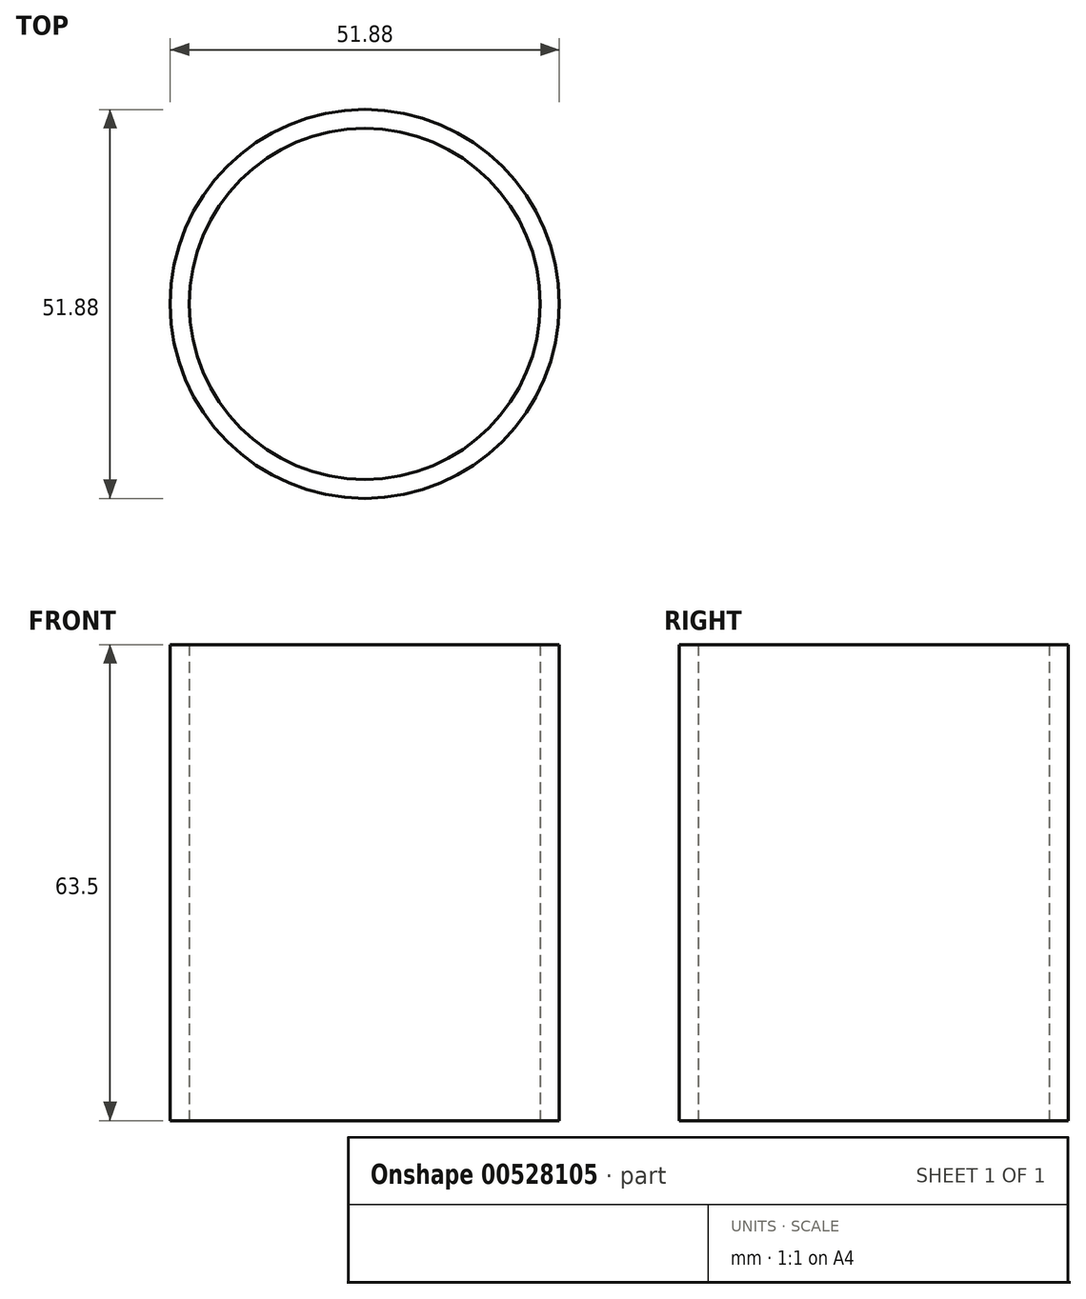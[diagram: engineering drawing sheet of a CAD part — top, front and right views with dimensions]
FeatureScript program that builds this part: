
annotation { "Feature Type Name" : "Feature", "Feature Type Description" : "" }
export const myFeature = defineFeature(function(context is Context, id is Id, definition is map)
    precondition{}
    {
        {
            var Q0;
            Q0=qCreatedBy(makeId("Top.planeOp"),FACE);
            var sketch = newSketch(context, id + "F0", { "sketchPlane" : qUnion([Q0])});
            skCircle(sketch, "E0", {"center": v(0, 0) * mm, "radius": 25.94 * mm});
            skSolve(sketch);
        }
        {
            var Q0;
            Q0=makeQuery(id+"F0.imprint","IMPRINT",FACE,{"disambiguationData":[TD([[makeQuery(id+"F0.imprint","IMPRINT",EDGE,{"derivedFrom":sQuery(id+"F0.wireOp",EDGE,"E0")}),1.0]])]});
            extrude(context, id + "F1", {"entities" : qUnion([Q0]), "depth" : 63.5 * mm, "offsetDistance" : 25.4 * mm});
        }
        {
            var Q0;
            Q0=makeQuery(id+"F1.opExtrude","CAP_FACE",FACE,{"disambiguationData":[OSD([sQuery(id+"F0.wireOp",EDGE,"E0")])],"isStart":false});
            var Q1;
            Q1=makeQuery(id+"F1.opExtrude","CAP_FACE",FACE,{"disambiguationData":[OSD([sQuery(id+"F0.wireOp",EDGE,"E0")])],"isStart":true});
            shell(context, id + "F2", {"entities" : qUnion([Q0, Q1]), "thickness" : 2.54 * mm});
        }
    });
